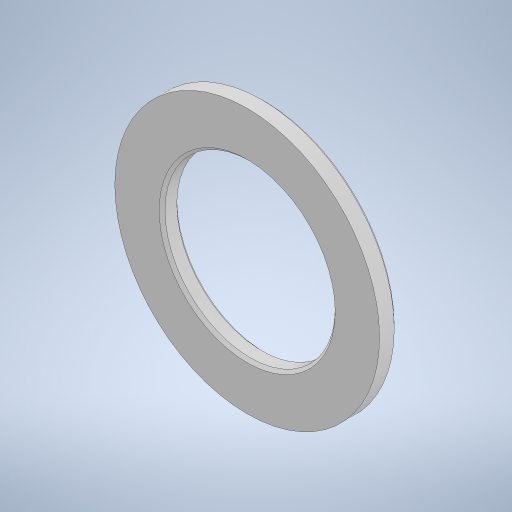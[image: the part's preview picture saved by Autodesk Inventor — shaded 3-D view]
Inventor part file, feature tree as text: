
AUTODESK INVENTOR PART (.ipt)
format: ipt  version: 2023 (Build 270158000, 158)  size: 406,016 bytes
history: native  units: mm
features: extrude x14, sketch x14, chamfer x3, projected_geometry x1
ambient origin geometry x8: Origin, YZ Plane, XZ Plane, XY Plane, X Axis, Y Axis, Z Axis, Center Point
bodies: Solid1 (feature_tree)
feature tree (32):
  extrude  "Extrusion1"  Depth=3.0mm TaperAngle=0.0deg
  extrude  "Extrusion2"  TaperAngle=0.0deg  [1 undecoded]
  chamfer  "Chamfer1"  Distance=0.5mm Angle=45.0deg
  extrude  "Extrusion3"  Depth=6.0mm TaperAngle=0.0deg
  extrude  "Extrusion4"  Depth=2.8mm TaperAngle=0.0deg
  extrude  "Extrusion5"  Depth=2.0mm TaperAngle=0.0deg
  extrude  "Extrusion6"  Depth=48.0mm
  extrude  "Extrusion7"  Depth=4.0mm
  extrude  "Extrusion8"  Depth=4.0mm
  chamfer  "Chamfer2"  Distance=4.8mm
  chamfer  "Chamfer3"  Distance=1.1mm Angle=45.0deg
  extrude  "Extrusion9"  Depth=23.0mm
  extrude  "Extrusion10"  Depth=10.0mm TaperAngle=360.0deg
  extrude  "Extrusion11"  TaperAngle=0.0deg  [1 undecoded]
  extrude  "Extrusion12"  Depth=10.0mm
  extrude  "Extrusion13"  Depth=10.0mm TaperAngle=360.0deg
  extrude  "Extrusion14"  Depth=10.0mm TaperAngle=0.0deg
  sketch  "Sketch1"  dims[d0=45.1mm d1=3.0mm d2=0.0mm]
  sketch  "Sketch2"  dims[d3=29.0mm d4=0.0mm d5=0.0mm d6=0.5mm d7=2.0mm d8=45.0deg]
  sketch  "Sketch3"  dims[d9=0.05mm d10=6.0mm d11=0.0mm]
  sketch  "Sketch4"  dims[d12=12.0mm d13=0.0mm d14=2.8mm d15=0.0mm]
  sketch  "Sketch5"  dims[d16=0.05mm d17=2.0mm d18=0.0mm]
  projected_geometry  "Projected Loop1"
  sketch  "Sketch6"  dims[d19=4.8mm d20=0.0mm d21=48.0mm]
  sketch  "Sketch7"  dims[d22=4.0mm d23=4.0mm]
  sketch  "Sketch8"  dims[d24=4.0mm d25=4.0mm]
  sketch  "Sketch9"  dims[d26=4.0mm]
  sketch  "Sketch10"  dims[d27=4.0mm]
  sketch  "Sketch12"  dims[d28=4.0mm]
  sketch  "Sketch14"  dims[d29=10.9mm d30=4.8mm d31=0.0mm d32=1.1mm d33=2.0mm d34=45.0deg]
  sketch  "Sketch15"  dims[d35=0.2mm d36=2.0mm d37=45.0deg d38=23.0mm]
  sketch  "Sketch16"  dims[d39=4.0mm d40=40.0mm d42=360.0deg d44=0.0mm d45=0.0mm d46=7.2mm d47=40.0mm d49=360.0deg d51=8.4mm d52=0.0mm d53=7.2mm d54=80.0mm d56=360.0deg d58=4.2mm d59=0.0mm d60=10.0mm d61=0.0mm d62=10.0mm d63=0.0mm d64=0.0mm d65=0.0mm]
note: 2 required parameter values undecoded (feature->parameter linkage not recoverable at this tier; creation-order binding heuristic only, values carry confidence <= 0.55)
